# Revit family: Toilet_Paper_Holder-American_Standard-Delancey-7455230_Series
name_source: partatom
category: Specialty Equipment
revit_build: Autodesk Revit 2014 (Build: 20130308_1515(x64)
units: mm (PartAtom-declared; Revit-internal decimal feet)

## types (4) — shared parameters
Assembly Code = C1030220
Default Elevation = 44"
Description = Delancey Toilet Paper Holder
Height = 2 3/16"
Installation Type = Wall Mounted
Length = 3 7/8"
Manufacturer = American Standard
Price = Prices may vary. Please consult Manufacturer Representative for most up-to-date price list.
URL = http://www.americanstandard-us.com
Warranty Information = 1 Year Warranty
Width = 7 1/8"

## per-type parameters (varying)
| type | Finish | Material |
| 7455230.002 | Metal-American Standard-002-Polished Chrome | Metal-American Standard-002-Polished Chrome |
| 7455230.295 | Metal-American Standard-295-Brushed Nickel | Metal-American Standard-295-Brushed Nickel |
| 7455230.013 | Metal-American Standard-013-Polished Nickel | Metal-American Standard-013-Polished Nickel |
| 7455230.278 | Metal-American Standard-278-Legacy Bronze | Metal-American Standard-278-Legacy Bronze |

note: column(s) folded — value = type name in every type: Model

## geometry (parser evidence)
native form markers: Sweep x1
no freeform markers — native parametric forms only
